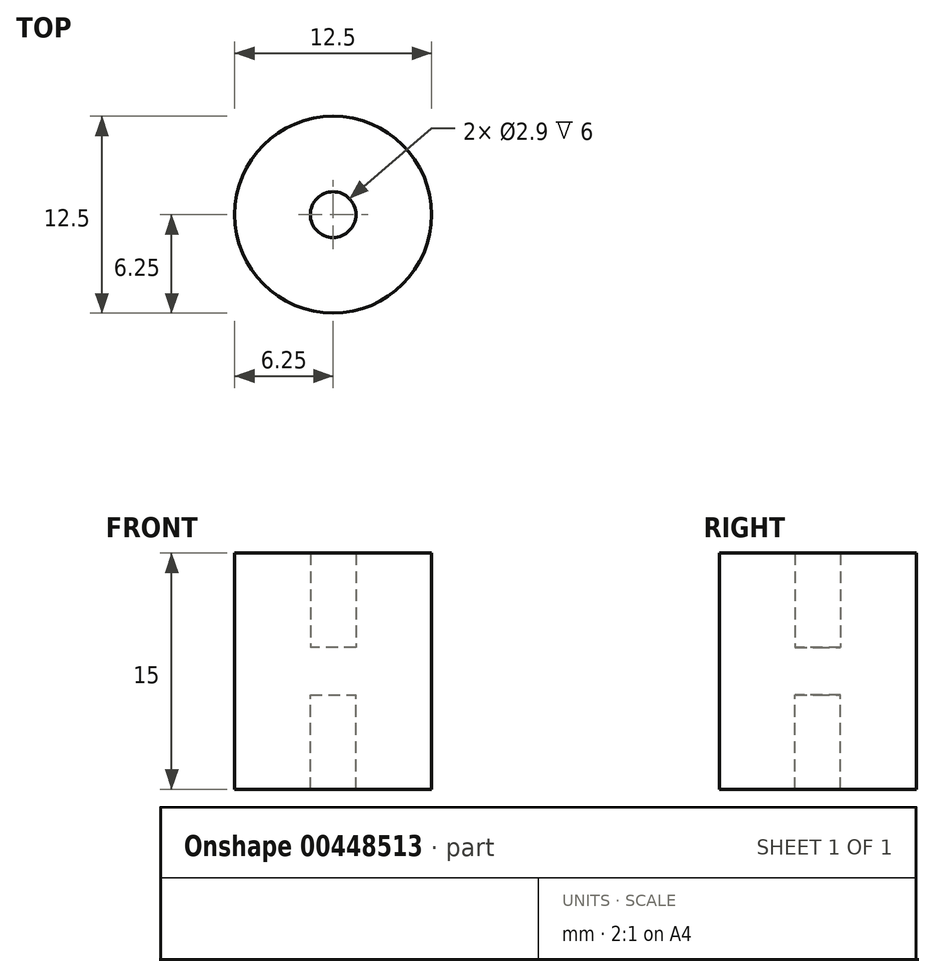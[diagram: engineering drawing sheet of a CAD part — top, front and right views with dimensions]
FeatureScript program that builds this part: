
annotation { "Feature Type Name" : "Feature", "Feature Type Description" : "" }
export const myFeature = defineFeature(function(context is Context, id is Id, definition is map)
    precondition{}
    {
        {
            var Q0;
            Q0=qCreatedBy(makeId("Top.planeOp"),FACE);
            var sketch = newSketch(context, id + "F0", { "sketchPlane" : qUnion([Q0])});
            skCircle(sketch, "E0", {"center": v(0, 0) * mm, "radius": 6.25 * mm});
            skSolve(sketch);
        }
        {
            var Q0;
            Q0=makeQuery(id+"F0.imprint","IMPRINT",FACE,{"disambiguationData":[TD([[makeQuery(id+"F0.imprint","IMPRINT",EDGE,{"derivedFrom":sQuery(id+"F0.wireOp",EDGE,"E0")}),1.0]])]});
            extrude(context, id + "F1", {"entities" : qUnion([Q0]), "depth" : 1.5 * mm, "hasSecondDirection" : true, "secondDirectionOppositeDirection" : true, "secondDirectionDepth" : 1.5 * mm});
        }
        {
            var Q0;
            Q0=makeQuery(id+"F1.opExtrude","CAP_FACE",FACE,{"disambiguationData":[OSD([sQuery(id+"F0.wireOp",EDGE,"E0")])],"isStart":false});
            var sketch = newSketch(context, id + "F2", { "sketchPlane" : qUnion([Q0])});
            skCircle(sketch, "E1", {"center": v(0, 0) * mm, "radius": 6.25 * mm});
            skCircle(sketch, "E2", {"center": v(0, 0) * mm, "radius": 1.45 * mm});
            skSolve(sketch);
        }
        {
            var Q0;
            Q0=makeQuery(id+"F2.imprint","IMPRINT",FACE,{"disambiguationData":[TD([[makeQuery(id+"F2.imprint","IMPRINT",EDGE,{"derivedFrom":sQuery(id+"F2.wireOp",EDGE,"E1")}),1.0]])]});
            extrude(context, id + "F3", {"entities" : qUnion([Q0]), "operationType" : NewBodyOperationType.ADD, "depth" : 6 * mm});
        }
        {
            var Q0;
            Q0=makeQuery(id+"F1.opExtrude","CAP_FACE",FACE,{"disambiguationData":[OSD([sQuery(id+"F0.wireOp",EDGE,"E0")])],"isStart":true});
            var sketch = newSketch(context, id + "F4", { "sketchPlane" : qUnion([Q0])});
            skCircle(sketch, "E3", {"center": v(0, 0) * mm, "radius": 6.25 * mm});
            skCircle(sketch, "E4", {"center": v(0, 0) * mm, "radius": 1.45 * mm});
            skSolve(sketch);
        }
        {
            var Q0;
            Q0=makeQuery(id+"F4.imprint","IMPRINT",FACE,{"disambiguationData":[TD([[makeQuery(id+"F4.imprint","IMPRINT",EDGE,{"derivedFrom":sQuery(id+"F4.wireOp",EDGE,"E3")}),-1.0]])]});
            extrude(context, id + "F5", {"entities" : qUnion([Q0]), "operationType" : NewBodyOperationType.ADD, "depth" : 6 * mm});
        }
    });
